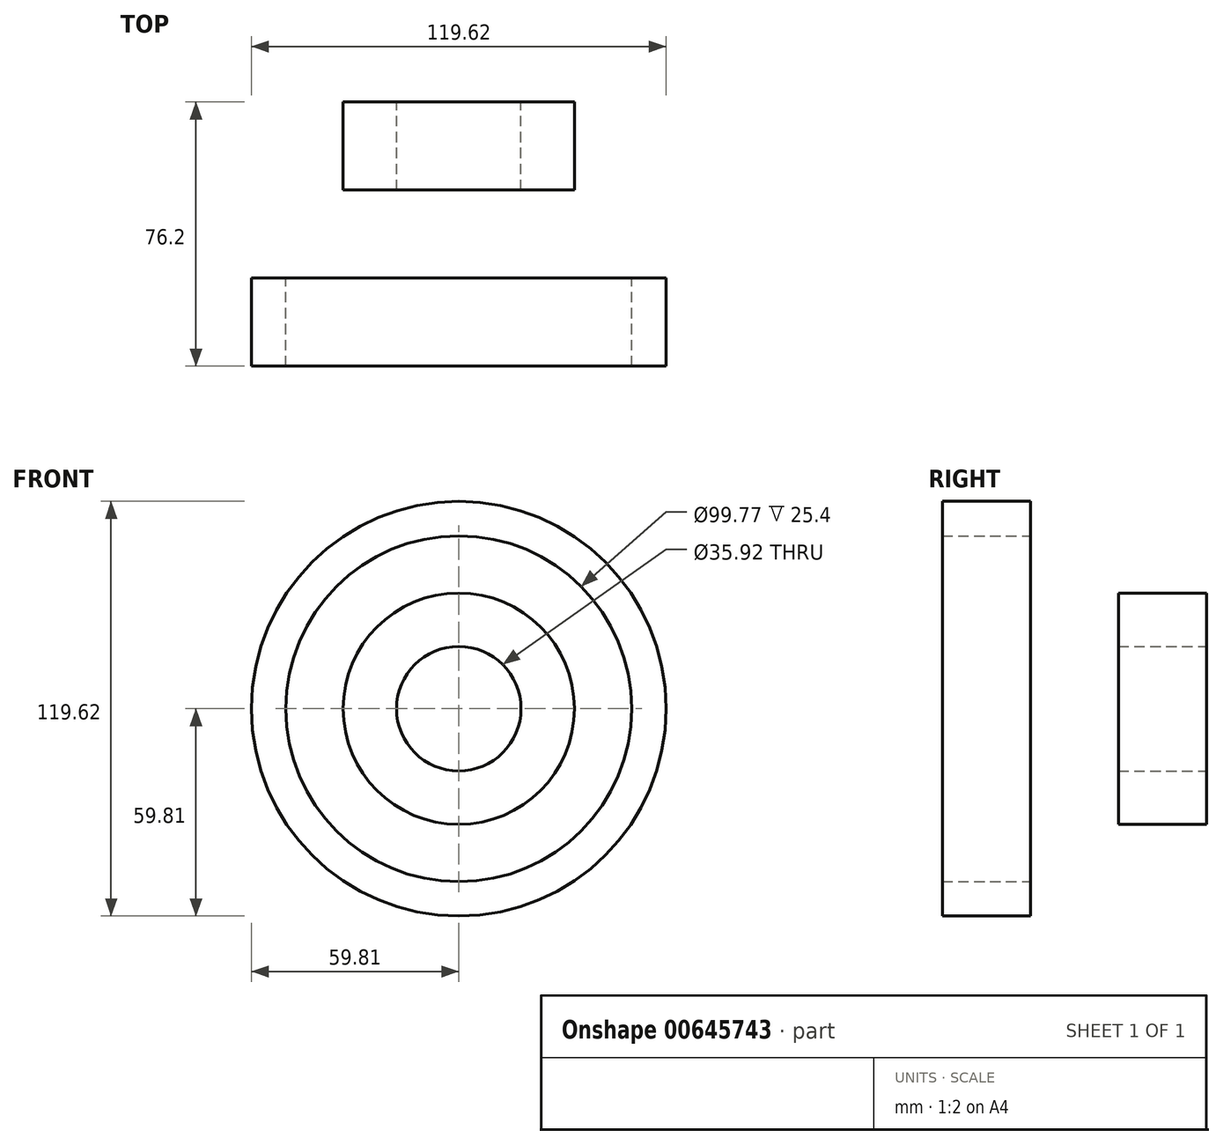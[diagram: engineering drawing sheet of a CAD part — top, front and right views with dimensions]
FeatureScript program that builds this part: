
annotation { "Feature Type Name" : "Feature", "Feature Type Description" : "" }
export const myFeature = defineFeature(function(context is Context, id is Id, definition is map)
    precondition{}
    {
        {
            var Q0;
            Q0=qCreatedBy(makeId("Front.planeOp"),FACE);
            var sketch = newSketch(context, id + "F0", { "sketchPlane" : qUnion([Q0])});
            skCircle(sketch, "E0", {"center": v(0, 0) * mm, "radius": 33.37 * mm});
            skCircle(sketch, "E1", {"center": v(0, 0) * mm, "radius": 17.96 * mm});
            skSolve(sketch);
        }
        {
            var Q0;
            Q0=qCreatedBy(makeId("Front.planeOp"),FACE);
            cPlane(context, id + "F1", {"entities" : qUnion([Q0]), "cplaneType" : CPlaneType.OFFSET, "offset" : 50.8 * mm, "width" : 152.4 * mm, "height" : 152.4 * mm});
        }
        {
            var Q0;
            Q0=makeQuery(id+"F0.imprint","IMPRINT",FACE,{"disambiguationData":[TD([[makeQuery(id+"F0.imprint","IMPRINT",EDGE,{"derivedFrom":sQuery(id+"F0.wireOp",EDGE,"E0")}),1.0]])]});
            extrude(context, id + "F2", {"entities" : qUnion([Q0]), "depth" : 25.4 * mm, "offsetDistance" : 25.4 * mm});
        }
        {
            var Q0;
            Q0=qCreatedBy(id+"F1.planeOp",FACE);
            var sketch = newSketch(context, id + "F3", { "sketchPlane" : qUnion([Q0])});
            skCircle(sketch, "E2", {"center": v(0, 0) * mm, "radius": 59.81 * mm});
            skCircle(sketch, "E3", {"center": v(0, 0) * mm, "radius": 49.88 * mm});
            skSolve(sketch);
        }
        {
            var Q0;
            Q0=makeQuery(id+"F3.imprint","IMPRINT",FACE,{"disambiguationData":[TD([[makeQuery(id+"F3.imprint","IMPRINT",EDGE,{"derivedFrom":sQuery(id+"F3.wireOp",EDGE,"E2")}),1.0]])]});
            extrude(context, id + "F4", {"entities" : qUnion([Q0]), "depth" : 25.4 * mm, "offsetDistance" : 25.4 * mm});
        }
        {
            var Q0;
            Q0=makeQuery(id+"F2.opExtrude","CAP_EDGE",EDGE,{"disambiguationData":[OSD([sQuery(id+"F0.wireOp",EDGE,"E1")])],"isStart":false});
            var Q1;
            Q1=makeQuery(id+"F4.opExtrude","CAP_EDGE",EDGE,{"disambiguationData":[OSD([sQuery(id+"F3.wireOp",EDGE,"E3")])],"isStart":true});
            loft(context, id + "F5", {"bodyType" : ToolBodyType.SURFACE, "wireProfilesArray" : [{ "wireProfileEntities" : qUnion([Q0]) }, { "wireProfileEntities" : qUnion([Q1]) }]});
        }
        {
            var Q0;
            Q0=makeQuery(id+"F2.opExtrude","CAP_EDGE",EDGE,{"disambiguationData":[OSD([sQuery(id+"F0.wireOp",EDGE,"E0")])],"isStart":false});
            var Q1;
            Q1=makeQuery(id+"F4.opExtrude","CAP_EDGE",EDGE,{"disambiguationData":[OSD([sQuery(id+"F3.wireOp",EDGE,"E2")])],"isStart":true});
            loft(context, id + "F6", {"bodyType" : ToolBodyType.SURFACE, "wireProfilesArray" : [{ "wireProfileEntities" : qUnion([Q0]) }, { "wireProfileEntities" : qUnion([Q1]) }]});
        }
    });
